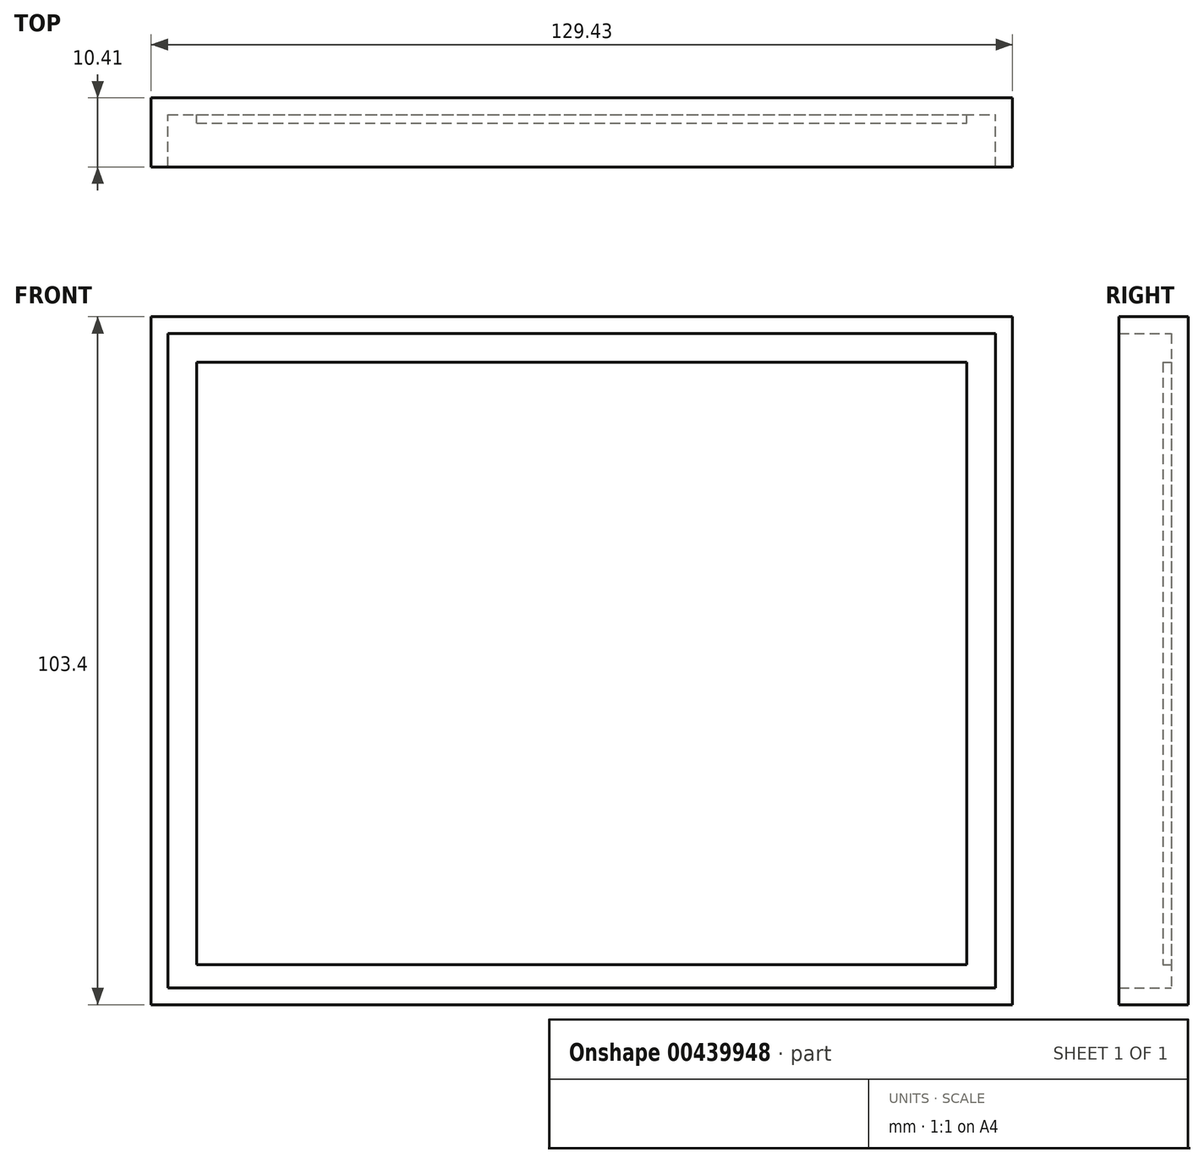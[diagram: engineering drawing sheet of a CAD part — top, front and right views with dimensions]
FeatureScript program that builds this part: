
annotation { "Feature Type Name" : "Feature", "Feature Type Description" : "" }
export const myFeature = defineFeature(function(context is Context, id is Id, definition is map)
    precondition{}
    {
        {
            var Q0;
            Q0=qCreatedBy(makeId("Front.planeOp"),FACE);
            var sketch = newSketch(context, id + "F0", { "sketchPlane" : qUnion([Q0])});
            skLineSegment(sketch, "E0.bottom", {"start": v(-67, 54.34) * mm, "end": v(62.43, 54.34) * mm});
            skLineSegment(sketch, "E0.top", {"start": v(-67, -49.06) * mm, "end": v(62.43, -49.06) * mm});
            skLineSegment(sketch, "E0.left", {"start": v(-67, 54.34) * mm, "end": v(-67, -49.06) * mm});
            skLineSegment(sketch, "E0.right", {"start": v(62.43, 54.34) * mm, "end": v(62.43, -49.06) * mm});
            skSolve(sketch);
        }
        {
            var Q0;
            Q0 = qSketchRegion(id + "F0", true);
            extrude(context, id + "F1", {"entities" : qUnion([Q0]), "depth" : 10.4 * mm});
        }
        {
            var Q0;
            Q0=makeQuery(id+"F1.opExtrude","CAP_FACE",FACE,{"disambiguationData":[OSD([sQuery(id+"F0.wireOp",EDGE,"E0.bottom"),sQuery(id+"F0.wireOp",EDGE,"E0.top"),sQuery(id+"F0.wireOp",EDGE,"E0.left"),sQuery(id+"F0.wireOp",EDGE,"E0.right")])],"isStart":false});
            shell(context, id + "F2", {"entities" : qUnion([Q0]), "thickness" : 2.54 * mm});
        }
        {
            var Q0;
            Q0=makeQuery(id+"F2.opShell","OFFSET_FACE",FACE,{"disambiguationData":[OSD([sQuery(id+"F0.wireOp",EDGE,"E0.bottom"),sQuery(id+"F0.wireOp",EDGE,"E0.top"),sQuery(id+"F0.wireOp",EDGE,"E0.left"),sQuery(id+"F0.wireOp",EDGE,"E0.right")])]});
            var sketch = newSketch(context, id + "F3", { "sketchPlane" : qUnion([Q0])});
            skLineSegment(sketch, "E1.bottom", {"start": v(-60.14, 47.48) * mm, "end": v(55.57, 47.48) * mm});
            skLineSegment(sketch, "E1.top", {"start": v(-60.14, -43.08) * mm, "end": v(55.57, -43.08) * mm});
            skLineSegment(sketch, "E1.left", {"start": v(-60.14, 47.48) * mm, "end": v(-60.14, -43.08) * mm});
            skLineSegment(sketch, "E1.right", {"start": v(55.57, 47.48) * mm, "end": v(55.57, -43.08) * mm});
            skSolve(sketch);
        }
        {
            var Q0;
            Q0 = qSketchRegion(id + "F3", true);
            extrude(context, id + "F4", {"entities" : qUnion([Q0]), "operationType" : NewBodyOperationType.ADD, "depth" : 1.27 * mm});
        }
    });
